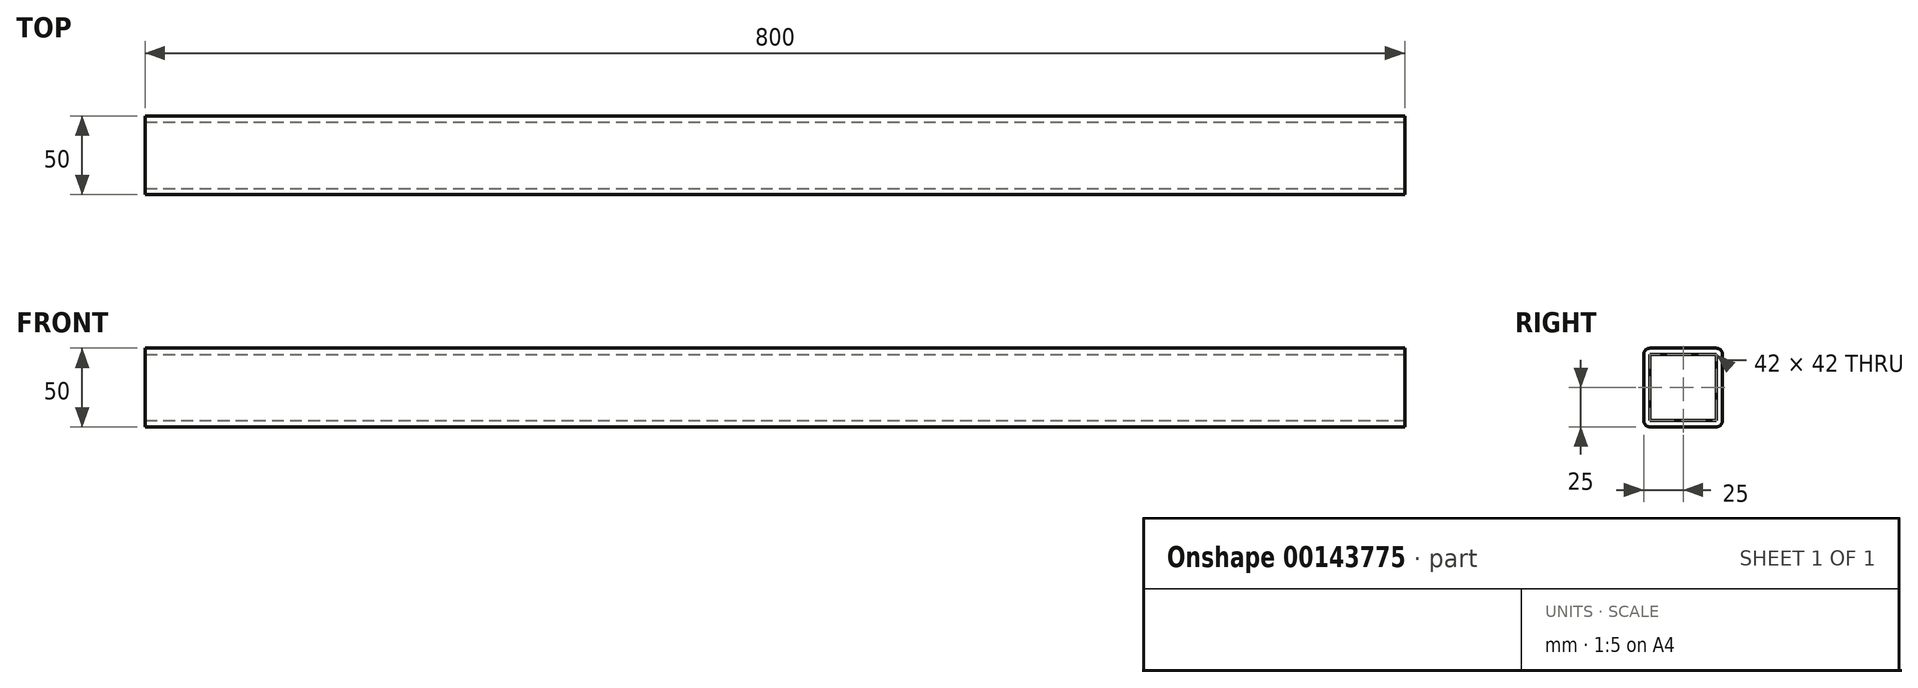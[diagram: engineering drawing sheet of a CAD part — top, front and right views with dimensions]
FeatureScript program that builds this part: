
annotation { "Feature Type Name" : "Feature", "Feature Type Description" : "" }
export const myFeature = defineFeature(function(context is Context, id is Id, definition is map)
    precondition{}
    {
        {
            var Q0;
            Q0=qCreatedBy(makeId("Right.planeOp"),FACE);
            var sketch = newSketch(context, id + "F0", { "sketchPlane" : qUnion([Q0])});
            skLineSegment(sketch, "E0.bottom", {"start": v(-21, 25) * mm, "end": v(21, 25) * mm});
            skLineSegment(sketch, "E0.top", {"start": v(-21, -25) * mm, "end": v(21, -25) * mm});
            skLineSegment(sketch, "E0.left", {"start": v(-25, 21) * mm, "end": v(-25, -21) * mm});
            skLineSegment(sketch, "E0.right", {"start": v(25, 21) * mm, "end": v(25, -21) * mm});
            skPoint(sketch, "E1.visualSharp", {"position": v(-25, 25) * mm});
            skArc(sketch, "E1.filletArc", {"start": v(-21, 25) * mm, "mid": v(-23.83, 23.83) * mm, "end": v(-25, 21) * mm});
            skPoint(sketch, "E2.visualSharp", {"position": v(-25, -25) * mm});
            skArc(sketch, "E2.filletArc", {"start": v(-25, -21) * mm, "mid": v(-23.83, -23.83) * mm, "end": v(-21, -25) * mm});
            skPoint(sketch, "E3.visualSharp", {"position": v(25, -25) * mm});
            skArc(sketch, "E3.filletArc", {"start": v(21, -25) * mm, "mid": v(23.83, -23.83) * mm, "end": v(25, -21) * mm});
            skPoint(sketch, "E4.visualSharp", {"position": v(25, 25) * mm});
            skArc(sketch, "E4.filletArc", {"start": v(25, 21) * mm, "mid": v(23.83, 23.83) * mm, "end": v(21, 25) * mm});
            skLineSegment(sketch, "E5.0", {"start": v(21, 21) * mm, "end": v(21, -21) * mm});
            skLineSegment(sketch, "E5.1", {"start": v(-21, 21) * mm, "end": v(21, 21) * mm});
            skLineSegment(sketch, "E5.2", {"start": v(-21, 21) * mm, "end": v(-21, -21) * mm});
            skLineSegment(sketch, "E5.3", {"start": v(-21, -21) * mm, "end": v(21, -21) * mm});
            skSolve(sketch);
        }
        {
            var Q0;
            Q0=makeQuery(id+"F0.imprint","IMPRINT",FACE,{"disambiguationData":[TD([[makeQuery(id+"F0.imprint","IMPRINT",EDGE,{"derivedFrom":sQuery(id+"F0.wireOp",EDGE,"E0.bottom")}),-1.0]])]});
            extrude(context, id + "F1", {"entities" : qUnion([Q0]), "endBound" : BoundingType.SYMMETRIC, "oppositeDirection" : true, "depth" : 800 * mm});
        }
    });
